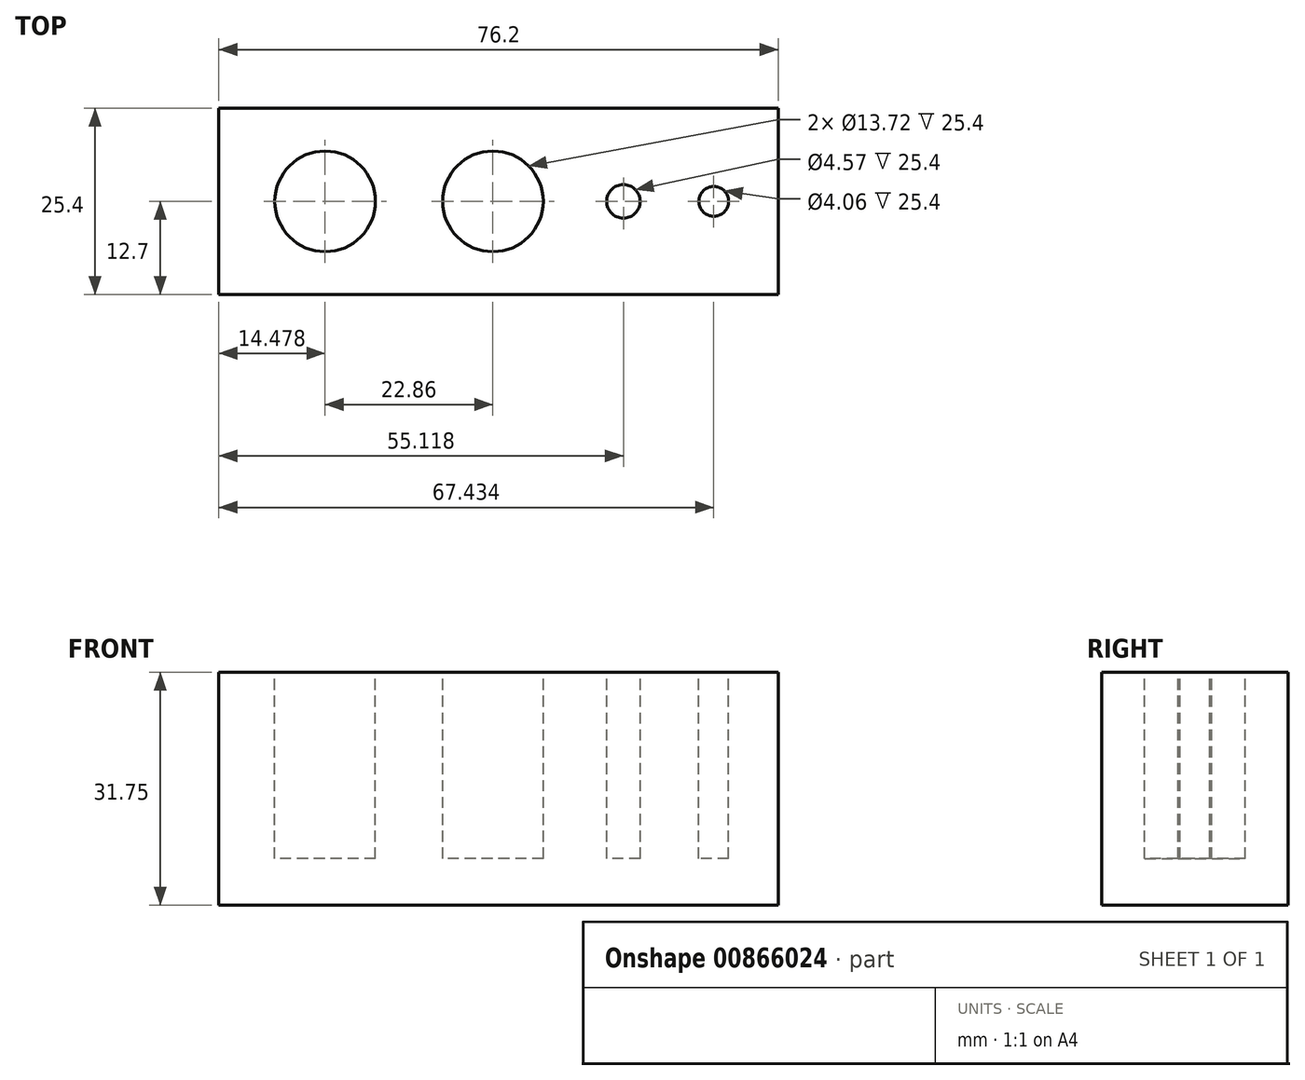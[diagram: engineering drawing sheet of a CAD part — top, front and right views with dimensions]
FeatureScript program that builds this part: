
annotation { "Feature Type Name" : "Feature", "Feature Type Description" : "" }
export const myFeature = defineFeature(function(context is Context, id is Id, definition is map)
    precondition{}
    {
        {
            var Q0;
            Q0=qCreatedBy(makeId("Top.planeOp"),FACE);
            var sketch = newSketch(context, id + "F0", { "sketchPlane" : qUnion([Q0])});
            skLineSegment(sketch, "E0.bottom", {"start": v(38.1, -12.7) * mm, "end": v(-38.1, -12.7) * mm});
            skLineSegment(sketch, "E0.top", {"start": v(38.1, 12.7) * mm, "end": v(-38.1, 12.7) * mm});
            skLineSegment(sketch, "E0.left", {"start": v(38.1, -12.7) * mm, "end": v(38.1, 12.7) * mm});
            skLineSegment(sketch, "E0.right", {"start": v(-38.1, -12.7) * mm, "end": v(-38.1, 12.7) * mm});
            skPoint(sketch, "E0.middle", {"position": v(0, 0) * mm});
            skSolve(sketch);
        }
        {
            var Q0;
            Q0 = qSketchRegion(id + "F0", true);
            extrude(context, id + "F1", {"entities" : qUnion([Q0]), "depth" : 31.75 * mm, "offsetDistance" : 25.4 * mm});
        }
        {
            var Q0;
            Q0=makeQuery(id+"F1.opExtrude","CAP_FACE",FACE,{"disambiguationData":[OSD([sQuery(id+"F0.wireOp",EDGE,"E0.bottom"),sQuery(id+"F0.wireOp",EDGE,"E0.top"),sQuery(id+"F0.wireOp",EDGE,"E0.left"),sQuery(id+"F0.wireOp",EDGE,"E0.right")])],"isStart":false});
            var sketch = newSketch(context, id + "F2", { "sketchPlane" : qUnion([Q0])});
            skLineSegment(sketch, "E1", {"start": v(0, 0) * mm, "end": v(96.77, 0) * mm});
            skPoint(sketch, "E1.endSnap0", {"position": v(38.1, 0) * mm});
            skLineSegment(sketch, "E2", {"start": v(0, 0) * mm, "end": v(-135.48, 0) * mm});
            skCircle(sketch, "E3", {"center": v(-23.62, 0) * mm, "radius": 6.86 * mm});
            skCircle(sketch, "E4", {"center": v(-0.76, 0) * mm, "radius": 6.86 * mm});
            skCircle(sketch, "E5", {"center": v(17.02, 0) * mm, "radius": 2.29 * mm});
            skCircle(sketch, "E6", {"center": v(29.33, 0) * mm, "radius": 2.03 * mm});
            skSolve(sketch);
        }
        {
            var Q0;
            Q0 = qSketchRegion(id + "F2", true);
            extrude(context, id + "F3", {"entities" : qUnion([Q0]), "operationType" : NewBodyOperationType.REMOVE, "oppositeDirection" : true, "depth" : 25.4 * mm, "offsetDistance" : 25.4 * mm});
        }
    });
